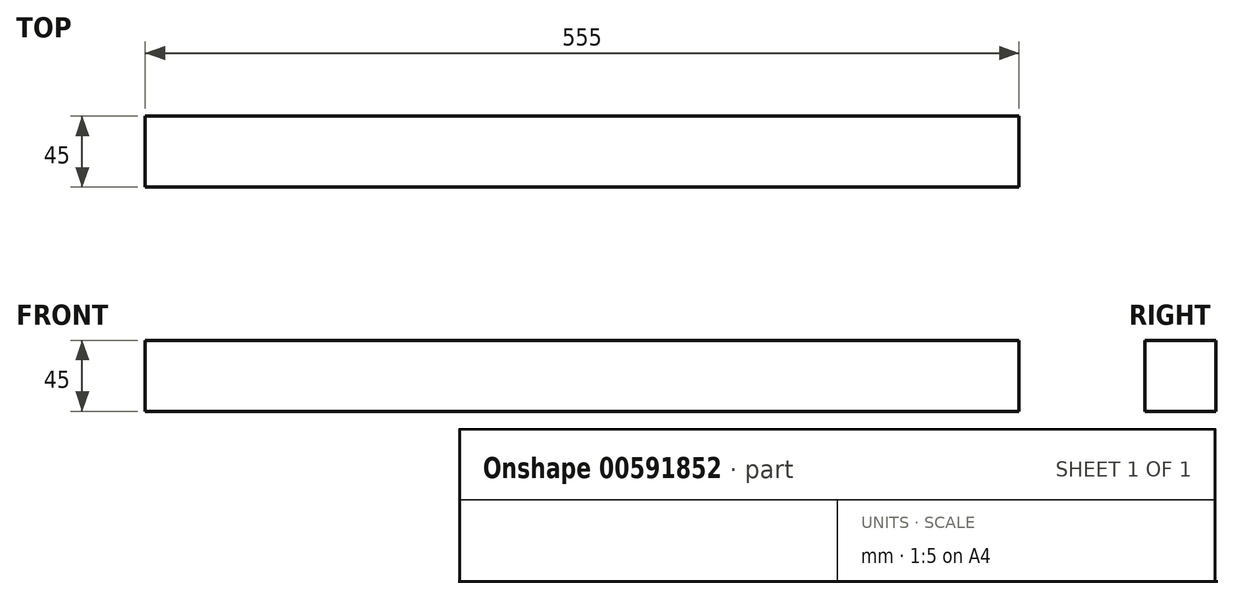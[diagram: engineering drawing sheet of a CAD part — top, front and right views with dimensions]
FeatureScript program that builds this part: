
annotation { "Feature Type Name" : "Feature", "Feature Type Description" : "" }
export const myFeature = defineFeature(function(context is Context, id is Id, definition is map)
    precondition{}
    {
        {
            var Q0;
            Q0=qCreatedBy(makeId("Right.planeOp"),FACE);
            var sketch = newSketch(context, id + "F0", { "sketchPlane" : qUnion([Q0])});
            skLineSegment(sketch, "E0.bottom", {"start": v(0, 0) * mm, "end": v(45, 0) * mm});
            skLineSegment(sketch, "E0.top", {"start": v(0, 45) * mm, "end": v(45, 45) * mm});
            skLineSegment(sketch, "E0.left", {"start": v(0, 0) * mm, "end": v(0, 45) * mm});
            skLineSegment(sketch, "E0.right", {"start": v(45, 0) * mm, "end": v(45, 45) * mm});
            skSolve(sketch);
        }
        {
            var Q0;
            Q0=makeQuery(id+"F0.imprint","IMPRINT",FACE,{"disambiguationData":[TD([[makeQuery(id+"F0.imprint","IMPRINT",EDGE,{"derivedFrom":sQuery(id+"F0.wireOp",EDGE,"E0.bottom")}),1.0]])]});
            extrude(context, id + "F1", {"entities" : qUnion([Q0]), "depth" : 555 * mm, "offsetDistance" : 25 * mm});
        }
    });
